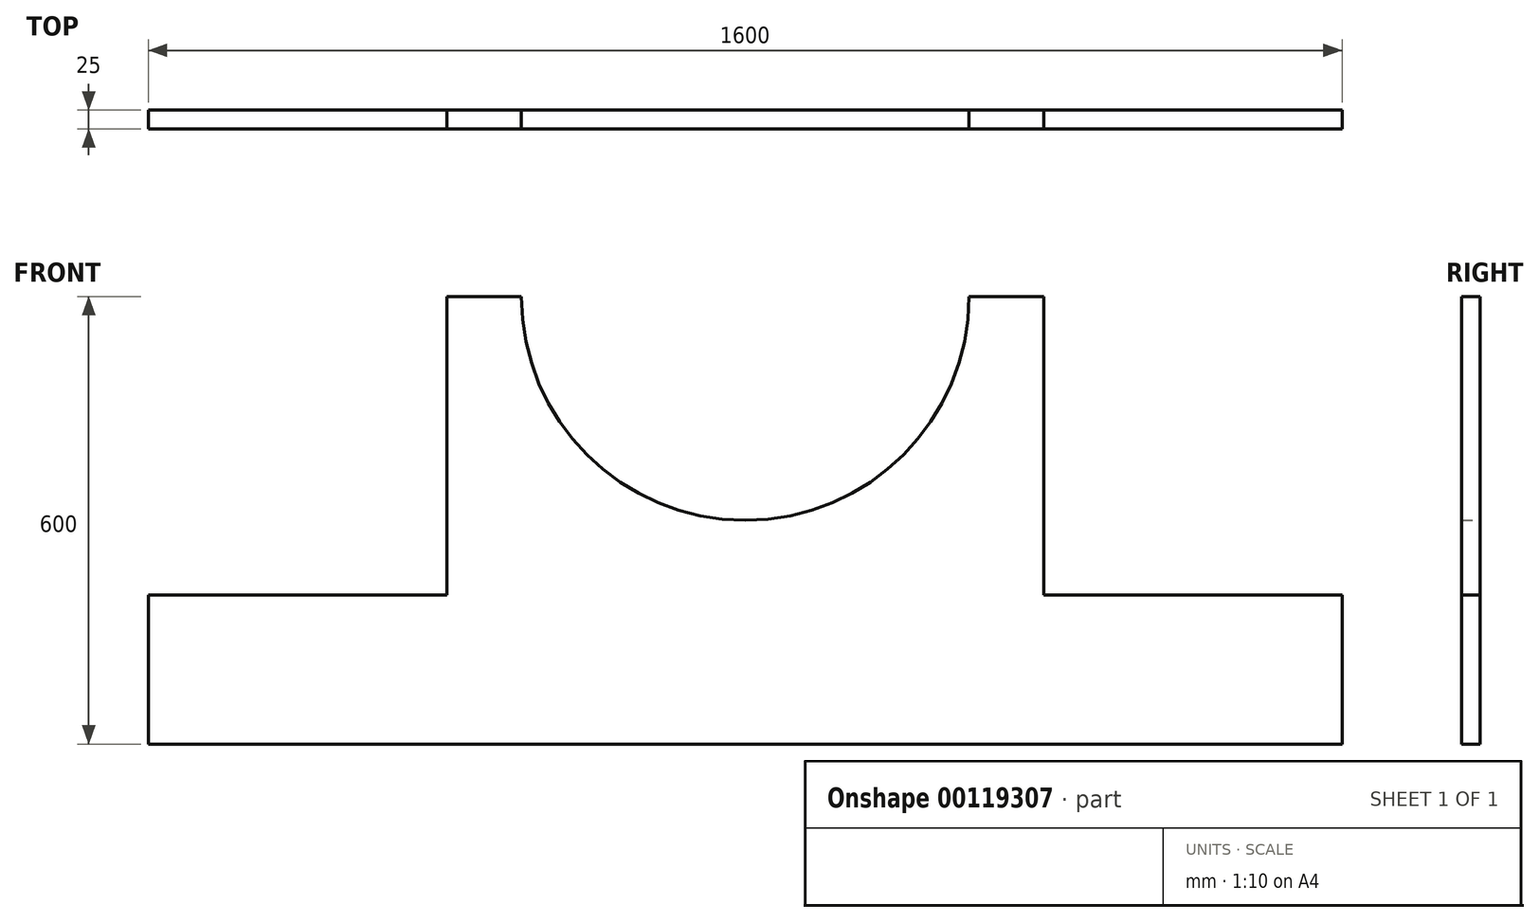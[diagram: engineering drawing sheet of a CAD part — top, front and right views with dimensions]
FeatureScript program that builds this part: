
annotation { "Feature Type Name" : "Feature", "Feature Type Description" : "" }
export const myFeature = defineFeature(function(context is Context, id is Id, definition is map)
    precondition{}
    {
        {
            var Q0;
            Q0=qCreatedBy(makeId("Front.planeOp"),FACE);
            var sketch = newSketch(context, id + "F0", { "sketchPlane" : qUnion([Q0])});
            skLineSegment(sketch, "E0.bottom", {"start": v(-800, -300) * mm, "end": v(800, -300) * mm});
            skLineSegment(sketch, "E0.left", {"start": v(-800, -300) * mm, "end": v(-800, -100) * mm});
            skLineSegment(sketch, "E0.right", {"start": v(800, -300) * mm, "end": v(800, -100) * mm});
            skPoint(sketch, "E0.middle", {"position": v(0, 0) * mm});
            skPoint(sketch, "E1.end.orphan", {"position": v(800, -150.75) * mm});
            skPoint(sketch, "E2.end.orphan", {"position": v(-540.15, 0) * mm});
            skPoint(sketch, "E3.end.orphan", {"position": v(-540.15, -150.75) * mm});
            skLineSegment(sketch, "E4", {"start": v(-800, -100) * mm, "end": v(-400, -100) * mm});
            skLineSegment(sketch, "E5", {"start": v(-400, -100) * mm, "end": v(-400, 300) * mm});
            skPoint(sketch, "E6.end.orphan", {"position": v(411.78, -100) * mm});
            skPoint(sketch, "E7.end.orphan", {"position": v(400, -100) * mm});
            skLineSegment(sketch, "E8", {"start": v(400, 300) * mm, "end": v(400, -100) * mm});
            skLineSegment(sketch, "E9", {"start": v(400, -100) * mm, "end": v(800, -100) * mm});
            skPoint(sketch, "E10.orphan", {"position": v(-800, 300) * mm});
            skPoint(sketch, "E11.orphan", {"position": v(800, 300) * mm});
            skPoint(sketch, "E12.center.orphan", {"position": v(0, 300) * mm});
            skArc(sketch, "E13", {"start": v(-300, 300) * mm, "mid": v(0, 0) * mm, "end": v(300, 300) * mm});
            skLineSegment(sketch, "E14", {"start": v(-400, 300) * mm, "end": v(-300, 300) * mm});
            skLineSegment(sketch, "E15", {"start": v(400, 300) * mm, "end": v(300, 300) * mm});
            skSolve(sketch);
        }
        {
            var Q0;
            Q0 = qSketchRegion(id + "F0", true);
            extrude(context, id + "F1", {"entities" : qUnion([Q0]), "depth" : 25 * mm});
        }
    });
